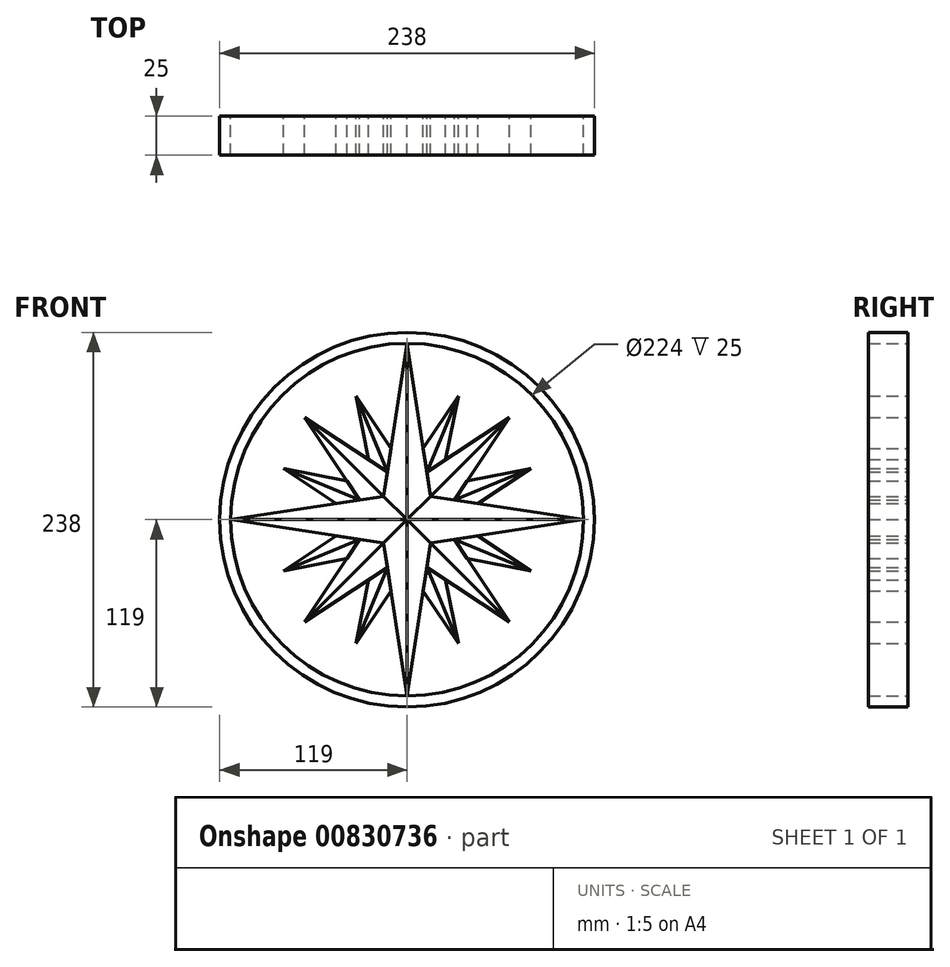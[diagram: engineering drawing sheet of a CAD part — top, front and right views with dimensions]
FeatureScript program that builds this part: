
annotation { "Feature Type Name" : "Feature", "Feature Type Description" : "" }
export const myFeature = defineFeature(function(context is Context, id is Id, definition is map)
    precondition{}
    {
        {
            var Q0;
            Q0=qCreatedBy(makeId("Front.planeOp"),FACE);
            var sketch = newSketch(context, id + "F0", { "sketchPlane" : qUnion([Q0])});
            skLineSegment(sketch, "E0", {"start": v(0, 0) * mm, "end": v(0, 112) * mm});
            skCircle(sketch, "E1", {"center": v(0, 0) * mm, "radius": 112 * mm});
            skLineSegment(sketch, "E2", {"start": v(0, 0) * mm, "end": v(112, 0) * mm});
            skLineSegment(sketch, "E3", {"start": v(0, 0) * mm, "end": v(14.85, 14.85) * mm});
            skLineSegment(sketch, "E4.1.0", {"start": v(0, 0) * mm, "end": v(-14.85, 14.85) * mm});
            skLineSegment(sketch, "E4.2.0", {"start": v(0, 0) * mm, "end": v(-14.85, -14.85) * mm});
            skLineSegment(sketch, "E4.3.0", {"start": v(0, 0) * mm, "end": v(14.85, -14.85) * mm});
            skLineSegment(sketch, "E5", {"start": v(14.85, 14.85) * mm, "end": v(0, 112) * mm});
            skLineSegment(sketch, "E6", {"start": v(0, 112) * mm, "end": v(-14.85, 14.85) * mm});
            skLineSegment(sketch, "E7", {"start": v(0, 0) * mm, "end": v(0, -112) * mm});
            skLineSegment(sketch, "E8", {"start": v(0, -112) * mm, "end": v(14.85, -14.85) * mm});
            skLineSegment(sketch, "E9", {"start": v(-14.85, -14.85) * mm, "end": v(0, -112) * mm});
            skLineSegment(sketch, "E10", {"start": v(14.85, 14.85) * mm, "end": v(112, 0) * mm});
            skLineSegment(sketch, "E11", {"start": v(112, 0) * mm, "end": v(14.85, -14.85) * mm});
            skLineSegment(sketch, "E12", {"start": v(0, 0) * mm, "end": v(-112, 0) * mm});
            skLineSegment(sketch, "E13", {"start": v(-112, 0) * mm, "end": v(-14.85, 14.85) * mm});
            skLineSegment(sketch, "E14", {"start": v(-112, 0) * mm, "end": v(-14.85, -14.85) * mm});
            skCircle(sketch, "E15", {"center": v(0, 0) * mm, "radius": 119 * mm});
            skArc(sketch, "E16", {"start": v(-65.05, 65.05) * mm, "mid": v(-36.62, 84.4) * mm, "end": v(-3.06, 91.95) * mm});
            skArc(sketch, "E17", {"start": v(65.05, 65.05) * mm, "mid": v(36.62, 84.4) * mm, "end": v(3.06, 91.95) * mm});
            skArc(sketch, "E18", {"start": v(65.05, 65.05) * mm, "mid": v(84.4, 36.62) * mm, "end": v(91.95, 3.06) * mm});
            skArc(sketch, "E19", {"start": v(65.05, -65.05) * mm, "mid": v(84.4, -36.62) * mm, "end": v(91.95, -3.06) * mm});
            skArc(sketch, "E20", {"start": v(-65.05, -65.05) * mm, "mid": v(-36.62, -84.4) * mm, "end": v(-3.06, -91.95) * mm});
            skArc(sketch, "E21", {"start": v(65.05, -65.05) * mm, "mid": v(36.62, -84.4) * mm, "end": v(3.06, -91.95) * mm});
            skArc(sketch, "E22", {"start": v(-65.05, 65.05) * mm, "mid": v(-84.4, 36.62) * mm, "end": v(-91.95, 3.06) * mm});
            skArc(sketch, "E23", {"start": v(-65.05, -65.05) * mm, "mid": v(-84.4, -36.62) * mm, "end": v(-91.95, -3.06) * mm});
            skLineSegment(sketch, "E24", {"start": v(-65.05, 65.05) * mm, "end": v(-14.85, 14.85) * mm});
            skLineSegment(sketch, "E25", {"start": v(-65.05, 65.05) * mm, "end": v(-12.5, 30.19) * mm});
            skLineSegment(sketch, "E26", {"start": v(-65.05, 65.05) * mm, "end": v(-30.19, 12.5) * mm});
            skLineSegment(sketch, "E27.1.0", {"start": v(-65.05, -65.05) * mm, "end": v(-12.5, -30.19) * mm});
            skLineSegment(sketch, "E27.1.1", {"start": v(-65.05, -65.05) * mm, "end": v(-14.85, -14.85) * mm});
            skLineSegment(sketch, "E27.1.2", {"start": v(-65.05, -65.05) * mm, "end": v(-30.19, -12.5) * mm});
            skLineSegment(sketch, "E27.2.0", {"start": v(65.05, -65.05) * mm, "end": v(30.19, -12.5) * mm});
            skLineSegment(sketch, "E27.2.1", {"start": v(65.05, -65.05) * mm, "end": v(14.85, -14.85) * mm});
            skLineSegment(sketch, "E27.2.2", {"start": v(65.05, -65.05) * mm, "end": v(12.5, -30.19) * mm});
            skLineSegment(sketch, "E27.3.0", {"start": v(65.05, 65.05) * mm, "end": v(12.5, 30.19) * mm});
            skLineSegment(sketch, "E27.3.1", {"start": v(65.05, 65.05) * mm, "end": v(14.85, 14.85) * mm});
            skLineSegment(sketch, "E27.3.2", {"start": v(65.05, 65.05) * mm, "end": v(30.19, 12.5) * mm});
            skLineSegment(sketch, "E28", {"start": v(-32.53, 78.53) * mm, "end": v(-12.5, 30.19) * mm});
            skLineSegment(sketch, "E29", {"start": v(32.53, -78.53) * mm, "end": v(24.5, -38.14) * mm});
            skLineSegment(sketch, "E30", {"start": v(32.53, -78.53) * mm, "end": v(10.22, -45.14) * mm});
            skLineSegment(sketch, "E31", {"start": v(-32.53, -78.53) * mm, "end": v(-10.22, -45.14) * mm});
            skLineSegment(sketch, "E32", {"start": v(-24.5, -38.14) * mm, "end": v(-32.53, -78.53) * mm});
            skLineSegment(sketch, "E33.1.0", {"start": v(78.53, 32.53) * mm, "end": v(38.14, 24.5) * mm});
            skLineSegment(sketch, "E33.1.2", {"start": v(78.53, 32.53) * mm, "end": v(45.14, 10.22) * mm});
            skLineSegment(sketch, "E33.2.0", {"start": v(-32.53, 78.53) * mm, "end": v(-24.5, 38.14) * mm});
            skLineSegment(sketch, "E33.2.2", {"start": v(-32.53, 78.53) * mm, "end": v(-10.22, 45.14) * mm});
            skLineSegment(sketch, "E33.3.0", {"start": v(-78.53, -32.53) * mm, "end": v(-38.14, -24.5) * mm});
            skLineSegment(sketch, "E33.3.2", {"start": v(-78.53, -32.53) * mm, "end": v(-45.14, -10.22) * mm});
            skLineSegment(sketch, "E34.1.1", {"start": v(38.14, -24.5) * mm, "end": v(78.53, -32.53) * mm});
            skLineSegment(sketch, "E34.1.2", {"start": v(78.53, -32.53) * mm, "end": v(45.14, -10.22) * mm});
            skLineSegment(sketch, "E34.2.1", {"start": v(24.5, 38.14) * mm, "end": v(32.53, 78.53) * mm});
            skLineSegment(sketch, "E34.2.2", {"start": v(32.53, 78.53) * mm, "end": v(10.22, 45.14) * mm});
            skLineSegment(sketch, "E34.3.1", {"start": v(-38.14, 24.5) * mm, "end": v(-78.53, 32.53) * mm});
            skLineSegment(sketch, "E34.3.2", {"start": v(-78.53, 32.53) * mm, "end": v(-45.14, 10.22) * mm});
            skLineSegment(sketch, "E35", {"start": v(-32.53, -78.53) * mm, "end": v(-12.5, -30.19) * mm});
            skLineSegment(sketch, "E36", {"start": v(32.53, -78.53) * mm, "end": v(12.5, -30.19) * mm});
            skLineSegment(sketch, "E37", {"start": v(78.53, -32.53) * mm, "end": v(30.19, -12.5) * mm});
            skLineSegment(sketch, "E38", {"start": v(78.53, 32.53) * mm, "end": v(30.19, 12.5) * mm});
            skLineSegment(sketch, "E39", {"start": v(32.53, 78.53) * mm, "end": v(12.5, 30.19) * mm});
            skLineSegment(sketch, "E40", {"start": v(-78.53, 32.53) * mm, "end": v(-30.19, 12.5) * mm});
            skLineSegment(sketch, "E41", {"start": v(-78.53, -32.53) * mm, "end": v(-30.19, -12.5) * mm});
            skSolve(sketch);
        }
        {
            var Q0;
            {var subQ3=sQuery(id+"F0.wireOp",EDGE,"E4.2.0");Q0=makeQuery(id+"F0.imprint","IMPRINT",FACE,{"disambiguationData":[TD([[makeQuery(id+"F0.imprint","IMPRINT",EDGE,{"derivedFrom":subQ3}),1.0]])]});}
            var Q1;
            {var subQ4=sQuery(id+"F0.wireOp",EDGE,"E4.1.0");Q1=makeQuery(id+"F0.imprint","IMPRINT",FACE,{"disambiguationData":[TD([[makeQuery(id+"F0.imprint","IMPRINT",EDGE,{"derivedFrom":subQ4}),1.0]])]});}
            var Q2;
            {var subQ3=sQuery(id+"F0.wireOp",EDGE,"E0");Q2=makeQuery(id+"F0.imprint","IMPRINT",FACE,{"disambiguationData":[TD([[makeQuery(id+"F0.imprint","IMPRINT",EDGE,{"derivedFrom":subQ3}),-1.0]])]});}
            var Q3;
            {var subQ3=sQuery(id+"F0.wireOp",EDGE,"E2");Q3=makeQuery(id+"F0.imprint","IMPRINT",FACE,{"disambiguationData":[TD([[makeQuery(id+"F0.imprint","IMPRINT",EDGE,{"derivedFrom":subQ3}),-1.0]])]});}
            var Q4;
            {var subQ0=sQuery(id+"F0.wireOp",EDGE,"E27.2.1");Q4=makeQuery(id+"F0.imprint","IMPRINT",FACE,{"disambiguationData":[TD([[makeQuery(id+"F0.imprint","IMPRINT",EDGE,{"derivedFrom":subQ0}),1.0]])]});}
            var Q5;
            {var subQ0=sQuery(id+"F0.wireOp",EDGE,"E27.1.1");Q5=makeQuery(id+"F0.imprint","IMPRINT",FACE,{"disambiguationData":[TD([[makeQuery(id+"F0.imprint","IMPRINT",EDGE,{"derivedFrom":subQ0}),1.0]])]});}
            var Q6;
            {var subQ0=sQuery(id+"F0.wireOp",EDGE,"E24");Q6=makeQuery(id+"F0.imprint","IMPRINT",FACE,{"disambiguationData":[TD([[makeQuery(id+"F0.imprint","IMPRINT",EDGE,{"derivedFrom":subQ0}),1.0]])]});}
            var Q7;
            {var subQ0=sQuery(id+"F0.wireOp",EDGE,"E27.3.1");Q7=makeQuery(id+"F0.imprint","IMPRINT",FACE,{"disambiguationData":[TD([[makeQuery(id+"F0.imprint","IMPRINT",EDGE,{"derivedFrom":subQ0}),1.0]])]});}
            var Q8;
            {var subQ2=sQuery(id+"F0.wireOp",EDGE,"E30");Q8=makeQuery(id+"F0.imprint","IMPRINT",FACE,{"disambiguationData":[TD([[makeQuery(id+"F0.imprint","IMPRINT",EDGE,{"derivedFrom":subQ2}),-1.0]])]});}
            var Q9;
            {var subQ2=sQuery(id+"F0.wireOp",EDGE,"E32");Q9=makeQuery(id+"F0.imprint","IMPRINT",FACE,{"disambiguationData":[TD([[makeQuery(id+"F0.imprint","IMPRINT",EDGE,{"derivedFrom":subQ2}),1.0]])]});}
            var Q10;
            {var subQ2=sQuery(id+"F0.wireOp",EDGE,"E33.3.2");Q10=makeQuery(id+"F0.imprint","IMPRINT",FACE,{"disambiguationData":[TD([[makeQuery(id+"F0.imprint","IMPRINT",EDGE,{"derivedFrom":subQ2}),-1.0]])]});}
            var Q11;
            {var subQ2=sQuery(id+"F0.wireOp",EDGE,"E34.3.1");Q11=makeQuery(id+"F0.imprint","IMPRINT",FACE,{"disambiguationData":[TD([[makeQuery(id+"F0.imprint","IMPRINT",EDGE,{"derivedFrom":subQ2}),1.0]])]});}
            var Q12;
            {var subQ2=sQuery(id+"F0.wireOp",EDGE,"E33.2.2");Q12=makeQuery(id+"F0.imprint","IMPRINT",FACE,{"disambiguationData":[TD([[makeQuery(id+"F0.imprint","IMPRINT",EDGE,{"derivedFrom":subQ2}),-1.0]])]});}
            var Q13;
            {var subQ2=sQuery(id+"F0.wireOp",EDGE,"E34.2.1");Q13=makeQuery(id+"F0.imprint","IMPRINT",FACE,{"disambiguationData":[TD([[makeQuery(id+"F0.imprint","IMPRINT",EDGE,{"derivedFrom":subQ2}),1.0]])]});}
            var Q14;
            {var subQ2=sQuery(id+"F0.wireOp",EDGE,"E33.1.2");Q14=makeQuery(id+"F0.imprint","IMPRINT",FACE,{"disambiguationData":[TD([[makeQuery(id+"F0.imprint","IMPRINT",EDGE,{"derivedFrom":subQ2}),-1.0]])]});}
            var Q15;
            {var subQ2=sQuery(id+"F0.wireOp",EDGE,"E34.1.1");Q15=makeQuery(id+"F0.imprint","IMPRINT",FACE,{"disambiguationData":[TD([[makeQuery(id+"F0.imprint","IMPRINT",EDGE,{"derivedFrom":subQ2}),1.0]])]});}
            var Q16;
            Q16=makeQuery(id+"F0.imprint","IMPRINT",FACE,{"disambiguationData":[TD([[makeQuery(id+"F0.imprint","IMPRINT",EDGE,{"derivedFrom":sQuery(id+"F0.wireOp",EDGE,"E15")}),1.0]])]});
            extrude(context, id + "F1", {"entities" : qUnion([Q0, Q1, Q2, Q3, Q4, Q5, Q6, Q7, Q8, Q9, Q10, Q11, Q12, Q13, Q14, Q15, Q16]), "depth" : 25 * mm, "offsetDistance" : 25 * mm});
        }
        {
            var Q0;
            {var subQ0=sQuery(id+"F0.wireOp",EDGE,"E24");Q0=makeQuery(id+"F0.imprint","IMPRINT",FACE,{"disambiguationData":[TD([[makeQuery(id+"F0.imprint","IMPRINT",EDGE,{"derivedFrom":subQ0}),-1.0]])]});}
            var Q1;
            {var subQ2=sQuery(id+"F0.wireOp",EDGE,"E33.2.0");Q1=makeQuery(id+"F0.imprint","IMPRINT",FACE,{"disambiguationData":[TD([[makeQuery(id+"F0.imprint","IMPRINT",EDGE,{"derivedFrom":subQ2}),1.0]])]});}
            var Q2;
            {var subQ1=sQuery(id+"F0.wireOp",EDGE,"E0");Q2=makeQuery(id+"F0.imprint","IMPRINT",FACE,{"disambiguationData":[TD([[makeQuery(id+"F0.imprint","IMPRINT",EDGE,{"derivedFrom":subQ1}),1.0]])]});}
            var Q3;
            {var subQ2=sQuery(id+"F0.wireOp",EDGE,"E34.2.2");Q3=makeQuery(id+"F0.imprint","IMPRINT",FACE,{"disambiguationData":[TD([[makeQuery(id+"F0.imprint","IMPRINT",EDGE,{"derivedFrom":subQ2}),1.0]])]});}
            var Q4;
            {var subQ0=sQuery(id+"F0.wireOp",EDGE,"E27.3.1");Q4=makeQuery(id+"F0.imprint","IMPRINT",FACE,{"disambiguationData":[TD([[makeQuery(id+"F0.imprint","IMPRINT",EDGE,{"derivedFrom":subQ0}),-1.0]])]});}
            var Q5;
            {var subQ4=sQuery(id+"F0.wireOp",EDGE,"E2");Q5=makeQuery(id+"F0.imprint","IMPRINT",FACE,{"disambiguationData":[TD([[makeQuery(id+"F0.imprint","IMPRINT",EDGE,{"derivedFrom":subQ4}),1.0]])]});}
            var Q6;
            {var subQ2=sQuery(id+"F0.wireOp",EDGE,"E33.1.0");Q6=makeQuery(id+"F0.imprint","IMPRINT",FACE,{"disambiguationData":[TD([[makeQuery(id+"F0.imprint","IMPRINT",EDGE,{"derivedFrom":subQ2}),1.0]])]});}
            var Q7;
            {var subQ2=sQuery(id+"F0.wireOp",EDGE,"E34.1.2");Q7=makeQuery(id+"F0.imprint","IMPRINT",FACE,{"disambiguationData":[TD([[makeQuery(id+"F0.imprint","IMPRINT",EDGE,{"derivedFrom":subQ2}),1.0]])]});}
            var Q8;
            {var subQ0=sQuery(id+"F0.wireOp",EDGE,"E27.2.1");Q8=makeQuery(id+"F0.imprint","IMPRINT",FACE,{"disambiguationData":[TD([[makeQuery(id+"F0.imprint","IMPRINT",EDGE,{"derivedFrom":subQ0}),-1.0]])]});}
            var Q9;
            {var subQ2=sQuery(id+"F0.wireOp",EDGE,"E29");Q9=makeQuery(id+"F0.imprint","IMPRINT",FACE,{"disambiguationData":[TD([[makeQuery(id+"F0.imprint","IMPRINT",EDGE,{"derivedFrom":subQ2}),1.0]])]});}
            var Q10;
            {var subQ3=sQuery(id+"F0.wireOp",EDGE,"E4.3.0");Q10=makeQuery(id+"F0.imprint","IMPRINT",FACE,{"disambiguationData":[TD([[makeQuery(id+"F0.imprint","IMPRINT",EDGE,{"derivedFrom":subQ3}),-1.0]])]});}
            var Q11;
            {var subQ2=sQuery(id+"F0.wireOp",EDGE,"E31");Q11=makeQuery(id+"F0.imprint","IMPRINT",FACE,{"disambiguationData":[TD([[makeQuery(id+"F0.imprint","IMPRINT",EDGE,{"derivedFrom":subQ2}),1.0]])]});}
            var Q12;
            {var subQ0=sQuery(id+"F0.wireOp",EDGE,"E27.1.1");Q12=makeQuery(id+"F0.imprint","IMPRINT",FACE,{"disambiguationData":[TD([[makeQuery(id+"F0.imprint","IMPRINT",EDGE,{"derivedFrom":subQ0}),-1.0]])]});}
            var Q13;
            {var subQ2=sQuery(id+"F0.wireOp",EDGE,"E33.3.0");Q13=makeQuery(id+"F0.imprint","IMPRINT",FACE,{"disambiguationData":[TD([[makeQuery(id+"F0.imprint","IMPRINT",EDGE,{"derivedFrom":subQ2}),1.0]])]});}
            var Q14;
            {var subQ3=sQuery(id+"F0.wireOp",EDGE,"E4.2.0");Q14=makeQuery(id+"F0.imprint","IMPRINT",FACE,{"disambiguationData":[TD([[makeQuery(id+"F0.imprint","IMPRINT",EDGE,{"derivedFrom":subQ3}),-1.0]])]});}
            var Q15;
            {var subQ2=sQuery(id+"F0.wireOp",EDGE,"E34.3.2");Q15=makeQuery(id+"F0.imprint","IMPRINT",FACE,{"disambiguationData":[TD([[makeQuery(id+"F0.imprint","IMPRINT",EDGE,{"derivedFrom":subQ2}),1.0]])]});}
            extrude(context, id + "F2", {"entities" : qUnion([Q0, Q1, Q2, Q3, Q4, Q5, Q6, Q7, Q8, Q9, Q10, Q11, Q12, Q13, Q14, Q15]), "depth" : 25 * mm, "offsetDistance" : 25 * mm});
        }
    });
